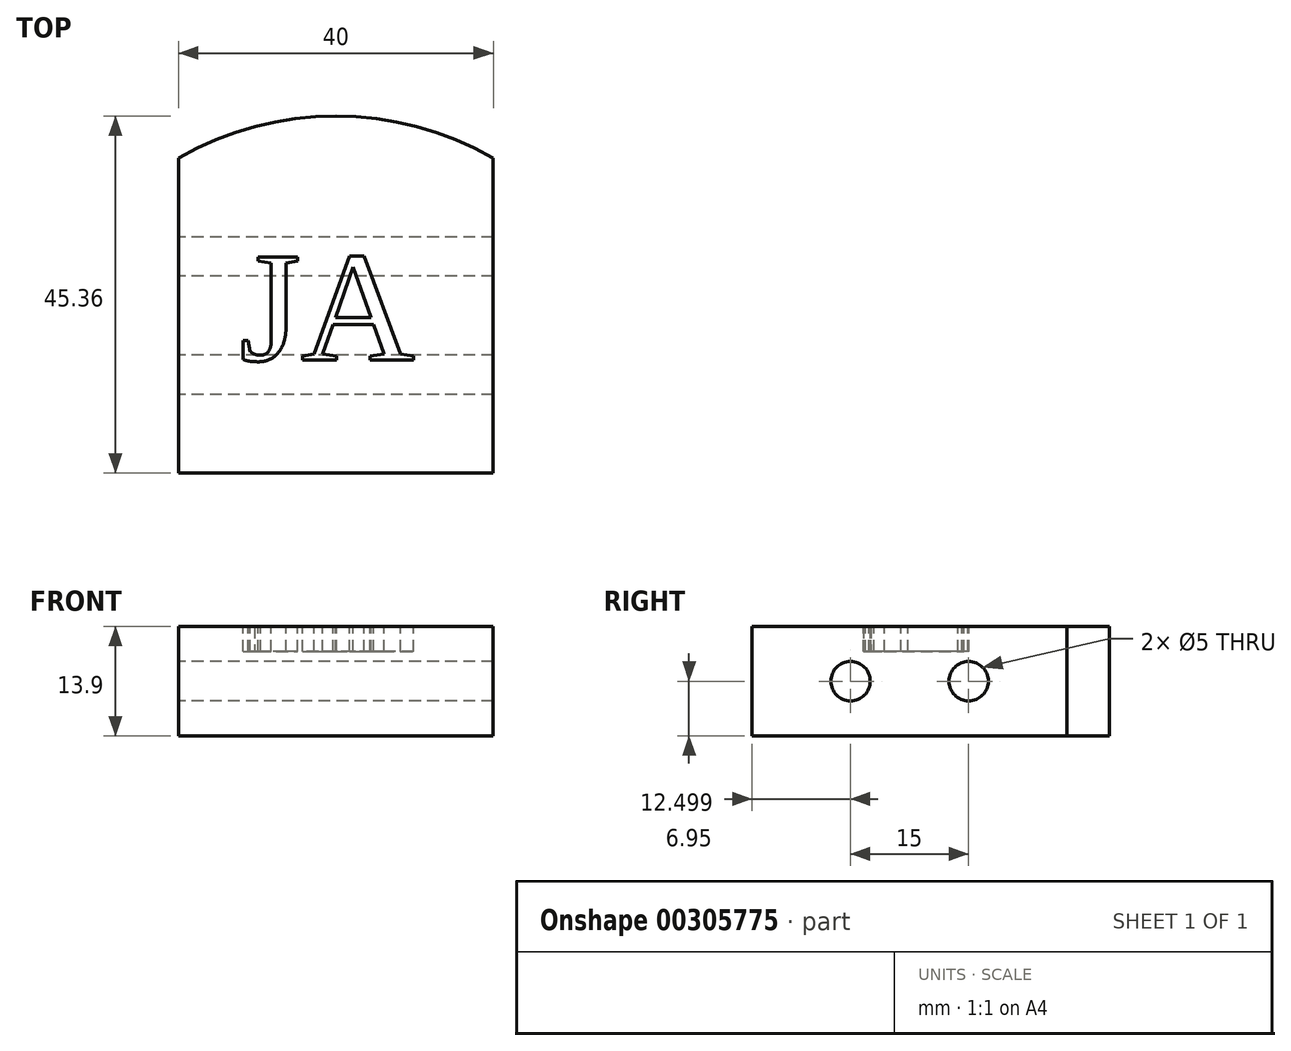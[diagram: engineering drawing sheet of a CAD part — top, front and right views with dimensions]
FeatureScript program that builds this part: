
annotation { "Feature Type Name" : "Feature", "Feature Type Description" : "" }
export const myFeature = defineFeature(function(context is Context, id is Id, definition is map)
    precondition{}
    {
        {
            var Q0;
            Q0=qCreatedBy(makeId("Top.planeOp"),FACE);
            var sketch = newSketch(context, id + "F0", { "sketchPlane" : qUnion([Q0])});
            skLineSegment(sketch, "E0.bottom", {"start": v(17.02, -47.54) * mm, "end": v(-22.98, -47.54) * mm});
            skLineSegment(sketch, "E0.top", {"start": v(17.02, -7.54) * mm, "end": v(-22.98, -7.54) * mm});
            skLineSegment(sketch, "E0.left", {"start": v(17.02, -47.54) * mm, "end": v(17.02, -7.54) * mm});
            skLineSegment(sketch, "E0.right", {"start": v(-22.98, -47.54) * mm, "end": v(-22.98, -7.54) * mm});
            skArc(sketch, "E1", {"start": v(17.02, -7.54) * mm, "mid": v(-2.98, -2.18) * mm, "end": v(-22.98, -7.54) * mm});
            skSolve(sketch);
        }
        {
            var Q0;
            Q0 = qSketchRegion(id + "F0", true);
            extrude(context, id + "F1", {"entities" : qUnion([Q0]), "depth" : 13.9 * mm});
        }
        {
            var Q0;
            Q0=makeQuery(id+"F1.opExtrude","SWEPT_FACE",FACE,{"disambiguationData":[OSD([sQuery(id+"F0.wireOp",EDGE,"E0.right")])]});
            var sketch = newSketch(context, id + "F2", { "sketchPlane" : qUnion([Q0])});
            skLineSegment(sketch, "E2", {"start": v(7.54, 6.95) * mm, "end": v(47.54, 6.95) * mm, "construction": true});
            skCircle(sketch, "E3", {"center": v(20.04, 6.95) * mm, "radius": 2.5 * mm});
            skCircle(sketch, "E4", {"center": v(35.04, 6.95) * mm, "radius": 2.5 * mm});
            skSolve(sketch);
        }
        {
            var Q0;
            Q0 = qSketchRegion(id + "F2", true);
            extrude(context, id + "F3", {"entities" : qUnion([Q0]), "operationType" : NewBodyOperationType.REMOVE, "oppositeDirection" : true, "depth" : 50 * mm});
        }
        {
            var Q0;
            Q0=makeQuery(id+"F1.opExtrude","CAP_FACE",FACE,{"disambiguationData":[OSD([sQuery(id+"F0.wireOp",EDGE,"E0.bottom"),sQuery(id+"F0.wireOp",EDGE,"E0.left"),sQuery(id+"F0.wireOp",EDGE,"E0.right"),sQuery(id+"F0.wireOp",EDGE,"E1")])],"isStart":false});
            var sketch = newSketch(context, id + "F4", { "sketchPlane" : qUnion([Q0])});
            skText(sketch, "E5", { "text": "JA", "fontName": "Tinos-Regular.ttf"});
            const initialGuessF4  = {"E5": [-0.0152, -0.03322, 1, 0, 0.01442]};
            skSetInitialGuess(sketch, initialGuessF4);
            skSolve(sketch);
        }
        {
            var Q0;
            Q0 = qSketchRegion(id + "F4", true);
            extrude(context, id + "F5", {"entities" : qUnion([Q0]), "operationType" : NewBodyOperationType.REMOVE, "oppositeDirection" : true, "depth" : 3.2 * mm});
        }
    });
